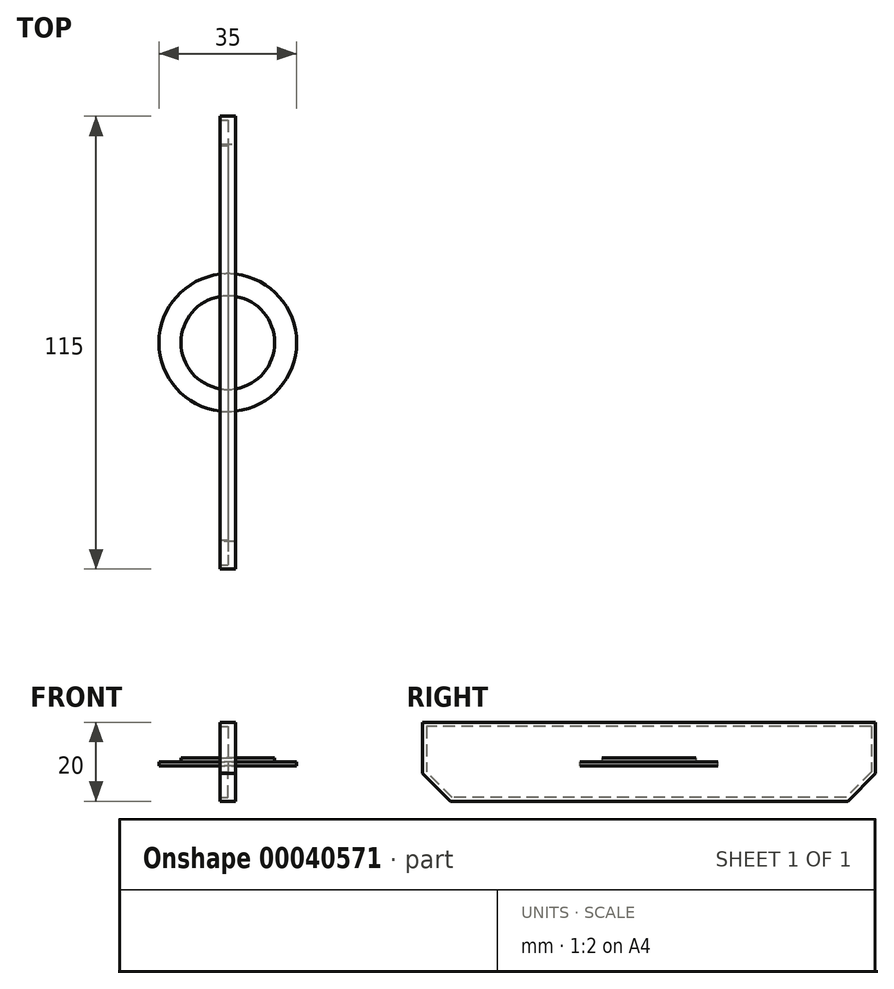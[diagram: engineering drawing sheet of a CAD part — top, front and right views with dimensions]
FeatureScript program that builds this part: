
annotation { "Feature Type Name" : "Feature", "Feature Type Description" : "" }
export const myFeature = defineFeature(function(context is Context, id is Id, definition is map)
    precondition{}
    {
        {
            var Q0;
            Q0=qCreatedBy(makeId("Top.planeOp"),FACE);
            var sketch = newSketch(context, id + "F0", { "sketchPlane" : qUnion([Q0])});
            skCircle(sketch, "E0", {"center": v(0, 0) * mm, "radius": 11.9 * mm});
            skSolve(sketch);
        }
        {
            var Q0;
            Q0=makeQuery(id+"F0.imprint","IMPRINT",FACE,{"disambiguationData":[TD([[makeQuery(id+"F0.imprint","IMPRINT",EDGE,{"derivedFrom":sQuery(id+"F0.wireOp",EDGE,"E0")}),1.0]])]});
            extrude(context, id + "F1", {"entities" : qUnion([Q0]), "depth" : 1 * mm});
        }
        {
            var Q0;
            Q0=makeQuery(id+"F1.opExtrude","CAP_FACE",FACE,{"disambiguationData":[OSD([sQuery(id+"F0.wireOp",EDGE,"E0")])],"isStart":true});
            var sketch = newSketch(context, id + "F2", { "sketchPlane" : qUnion([Q0])});
            skCircle(sketch, "E1", {"center": v(0, 0) * mm, "radius": 17.5 * mm});
            skSolve(sketch);
        }
        {
            var Q0;
            Q0 = qSketchRegion(id + "F2", true);
            extrude(context, id + "F3", {"entities" : qUnion([Q0]), "operationType" : NewBodyOperationType.ADD, "depth" : 1 * mm});
        }
        {
            var Q0;
            Q0=qCreatedBy(makeId("Right.planeOp"),FACE);
            var sketch = newSketch(context, id + "F4", { "sketchPlane" : qUnion([Q0])});
            skLineSegment(sketch, "E2.rect.bottom", {"start": v(57.5, 10) * mm, "end": v(-57.5, 10) * mm});
            skLineSegment(sketch, "E2.rect.top", {"start": v(57.5, -10) * mm, "end": v(-57.5, -10) * mm});
            skLineSegment(sketch, "E2.rect.left", {"start": v(57.5, 10) * mm, "end": v(57.5, -10) * mm});
            skLineSegment(sketch, "E2.rect.right", {"start": v(-57.5, 10) * mm, "end": v(-57.5, -10) * mm});
            skPoint(sketch, "E2.rect.middle", {"position": v(0, 0) * mm});
            skSolve(sketch);
        }
        {
            var Q0;
            Q0=makeQuery(id+"F4.imprint","IMPRINT",FACE,{"disambiguationData":[TD([[makeQuery(id+"F4.imprint","IMPRINT",EDGE,{"derivedFrom":sQuery(id+"F4.wireOp",EDGE,"E2.rect.bottom")}),1.0]])]});
            extrude(context, id + "F5", {"entities" : qUnion([Q0]), "depth" : 2 * mm});
        }
        {
            var Q0;
            Q0=makeQuery(id+"F5.opExtrude","SWEPT_EDGE",EDGE,{"disambiguationData":[OSD([sQuery(id+"F4.wireOp",EDGE,"E2.rect.top"),sQuery(id+"F4.wireOp",EDGE,"E2.rect.right")])]});
            var Q1;
            Q1=makeQuery(id+"F5.opExtrude","SWEPT_EDGE",EDGE,{"disambiguationData":[OSD([sQuery(id+"F4.wireOp",EDGE,"E2.rect.top"),sQuery(id+"F4.wireOp",EDGE,"E2.rect.left")])]});
            chamfer(context, id + "F6", {"entities" : qUnion([Q0, Q1]), "width" : 7 * mm, "tangentPropagation" : true});
        }
        {
            var Q0;
            Q0=makeQuery(id+"F5.opExtrude","CAP_FACE",FACE,{"disambiguationData":[OSD([sQuery(id+"F4.wireOp",EDGE,"E2.rect.bottom"),sQuery(id+"F4.wireOp",EDGE,"E2.rect.top"),sQuery(id+"F4.wireOp",EDGE,"E2.rect.left"),sQuery(id+"F4.wireOp",EDGE,"E2.rect.right")])],"isStart":true});
            var sketch = newSketch(context, id + "F7", { "sketchPlane" : qUnion([Q0])});
            skLineSegment(sketch, "E3.0", {"start": v(-57.5, 10) * mm, "end": v(57.5, 10) * mm});
            skLineSegment(sketch, "E3.1", {"start": v(-57.5, 10) * mm, "end": v(-57.5, -3) * mm});
            skLineSegment(sketch, "E3.2", {"start": v(-57.5, -3) * mm, "end": v(-50.5, -10) * mm});
            skLineSegment(sketch, "E3.3", {"start": v(-50.5, -10) * mm, "end": v(50.5, -10) * mm});
            skLineSegment(sketch, "E3.4", {"start": v(50.5, -10) * mm, "end": v(57.5, -3) * mm});
            skLineSegment(sketch, "E3.5", {"start": v(57.5, 10) * mm, "end": v(57.5, -3) * mm});
            skLineSegment(sketch, "E4.0", {"start": v(-56.5, 9) * mm, "end": v(-56.5, -2.59) * mm});
            skLineSegment(sketch, "E4.1", {"start": v(56.5, 9) * mm, "end": v(56.5, -2.59) * mm});
            skLineSegment(sketch, "E4.2", {"start": v(50.09, -9) * mm, "end": v(56.5, -2.59) * mm});
            skLineSegment(sketch, "E4.3", {"start": v(-56.5, 9) * mm, "end": v(56.5, 9) * mm});
            skLineSegment(sketch, "E4.4", {"start": v(-50.09, -9) * mm, "end": v(50.09, -9) * mm});
            skLineSegment(sketch, "E4.5", {"start": v(-56.5, -2.59) * mm, "end": v(-50.09, -9) * mm});
            skSolve(sketch);
        }
        {
            var Q0;
            Q0 = qSketchRegion(id + "F7", true);
            extrude(context, id + "F8", {"entities" : qUnion([Q0]), "operationType" : NewBodyOperationType.ADD, "depth" : 2 * mm});
        }
    });
